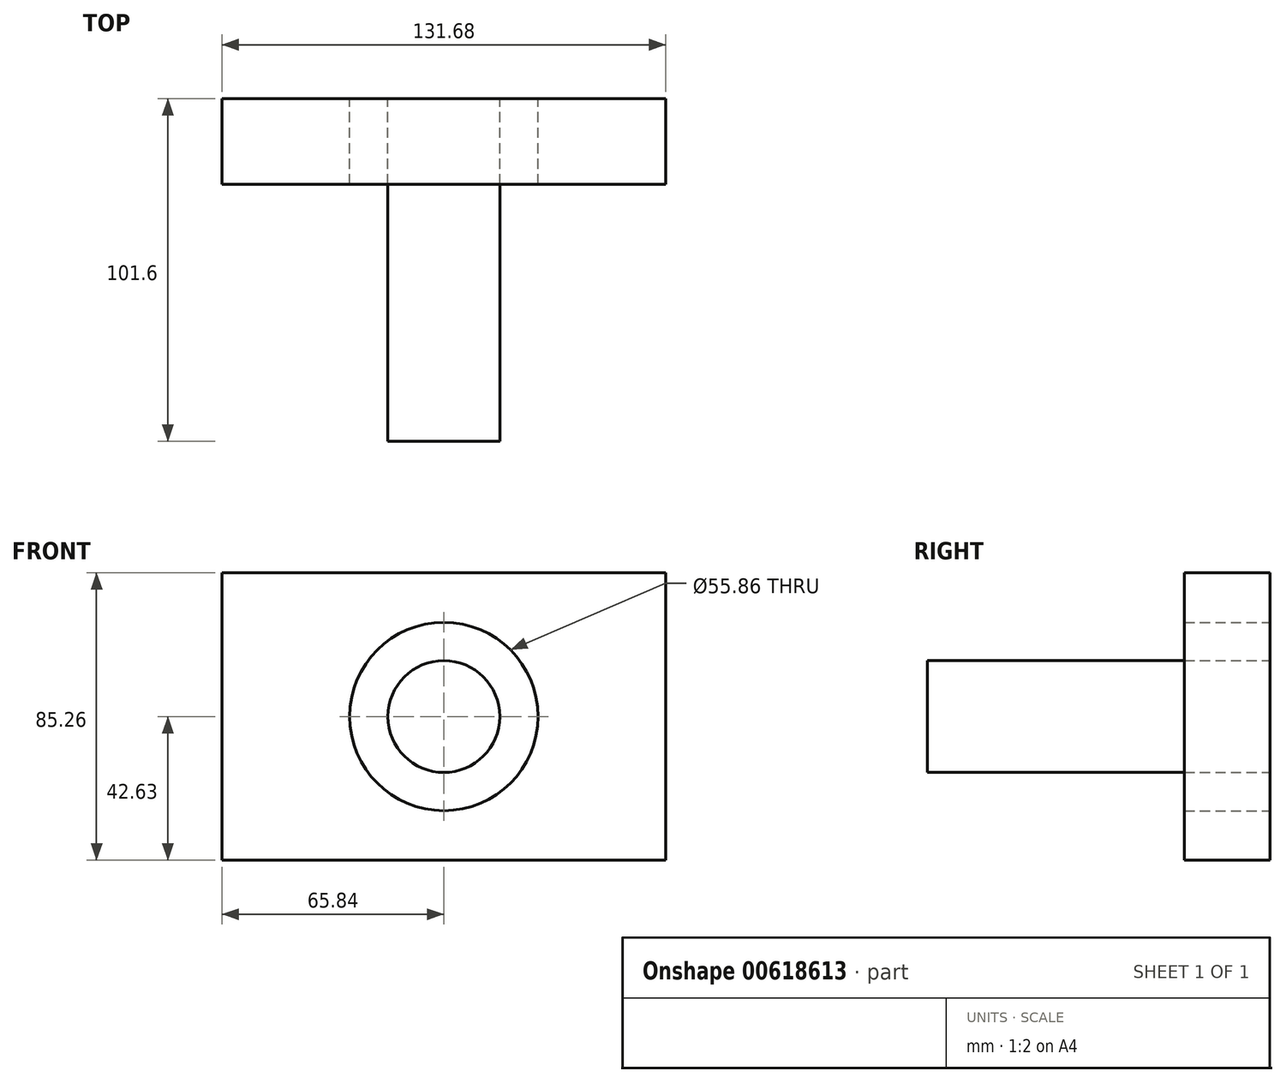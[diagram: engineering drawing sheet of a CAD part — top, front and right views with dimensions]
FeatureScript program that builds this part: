
annotation { "Feature Type Name" : "Feature", "Feature Type Description" : "" }
export const myFeature = defineFeature(function(context is Context, id is Id, definition is map)
    precondition{}
    {
        {
            var Q0;
            Q0=qCreatedBy(makeId("Front.planeOp"),FACE);
            var sketch = newSketch(context, id + "F0", { "sketchPlane" : qUnion([Q0])});
            skLineSegment(sketch, "E0.bottom", {"start": v(-65.84, 42.63) * mm, "end": v(65.84, 42.63) * mm});
            skLineSegment(sketch, "E0.top", {"start": v(-65.84, -42.63) * mm, "end": v(65.84, -42.63) * mm});
            skLineSegment(sketch, "E0.left", {"start": v(-65.84, 42.63) * mm, "end": v(-65.84, -42.63) * mm});
            skLineSegment(sketch, "E0.right", {"start": v(65.84, 42.63) * mm, "end": v(65.84, -42.63) * mm});
            skPoint(sketch, "E0.middle", {"position": v(0, 0) * mm});
            skCircle(sketch, "E1", {"center": v(0, 0) * mm, "radius": 27.93 * mm});
            skLineSegment(sketch, "E2.bottom", {"start": v(40.83, 27.93) * mm, "end": v(-40.83, 27.93) * mm});
            skLineSegment(sketch, "E2.top", {"start": v(40.83, -27.93) * mm, "end": v(-40.83, -27.93) * mm});
            skLineSegment(sketch, "E2.left", {"start": v(40.83, 27.93) * mm, "end": v(40.83, -27.93) * mm});
            skLineSegment(sketch, "E2.right", {"start": v(-40.83, 27.93) * mm, "end": v(-40.83, -27.93) * mm});
            skLineSegment(sketch, "E3", {"start": v(40.83, 27.93) * mm, "end": v(40.83, 42.63) * mm, "construction": true});
            skLineSegment(sketch, "E4", {"start": v(40.83, 27.93) * mm, "end": v(65.84, 27.93) * mm, "construction": true});
            skLineSegment(sketch, "E5", {"start": v(40.83, -27.93) * mm, "end": v(40.83, -42.63) * mm, "construction": true});
            skLineSegment(sketch, "E6", {"start": v(40.83, -27.93) * mm, "end": v(65.84, -27.93) * mm, "construction": true});
            skLineSegment(sketch, "E7", {"start": v(-40.83, 27.93) * mm, "end": v(-65.84, 27.93) * mm, "construction": true});
            skCircle(sketch, "E8", {"center": v(0, 0) * mm, "radius": 16.6 * mm});
            skSolve(sketch);
        }
        {
            var Q0;
            Q0 = qSketchRegion(id + "F0", true);
            var Q1;
            {var subQ5=sQuery(id+"F0.wireOp",EDGE,"E2.left");Q1=makeQuery(id+"F0.imprint","IMPRINT",FACE,{"disambiguationData":[TD([[makeQuery(id+"F0.imprint","IMPRINT",EDGE,{"derivedFrom":subQ5}),-1.0]])]});}
            var Q2;
            {var subQ5=sQuery(id+"F0.wireOp",EDGE,"E2.right");Q2=makeQuery(id+"F0.imprint","IMPRINT",FACE,{"disambiguationData":[TD([[makeQuery(id+"F0.imprint","IMPRINT",EDGE,{"derivedFrom":subQ5}),1.0]])]});}
            extrude(context, id + "F1", {"entities" : qUnion([Q0, Q1, Q2]), "depth" : 25.4 * mm, "offsetDistance" : 25.4 * mm});
        }
        {
            var Q0;
            Q0=makeQuery(id+"F0.imprint","IMPRINT",FACE,{"disambiguationData":[TD([[makeQuery(id+"F0.imprint","IMPRINT",EDGE,{"derivedFrom":sQuery(id+"F0.wireOp",EDGE,"E8")}),1.0]])]});
            extrude(context, id + "F2", {"entities" : qUnion([Q0]), "depth" : 101.6 * mm, "offsetDistance" : 25.4 * mm});
        }
    });
